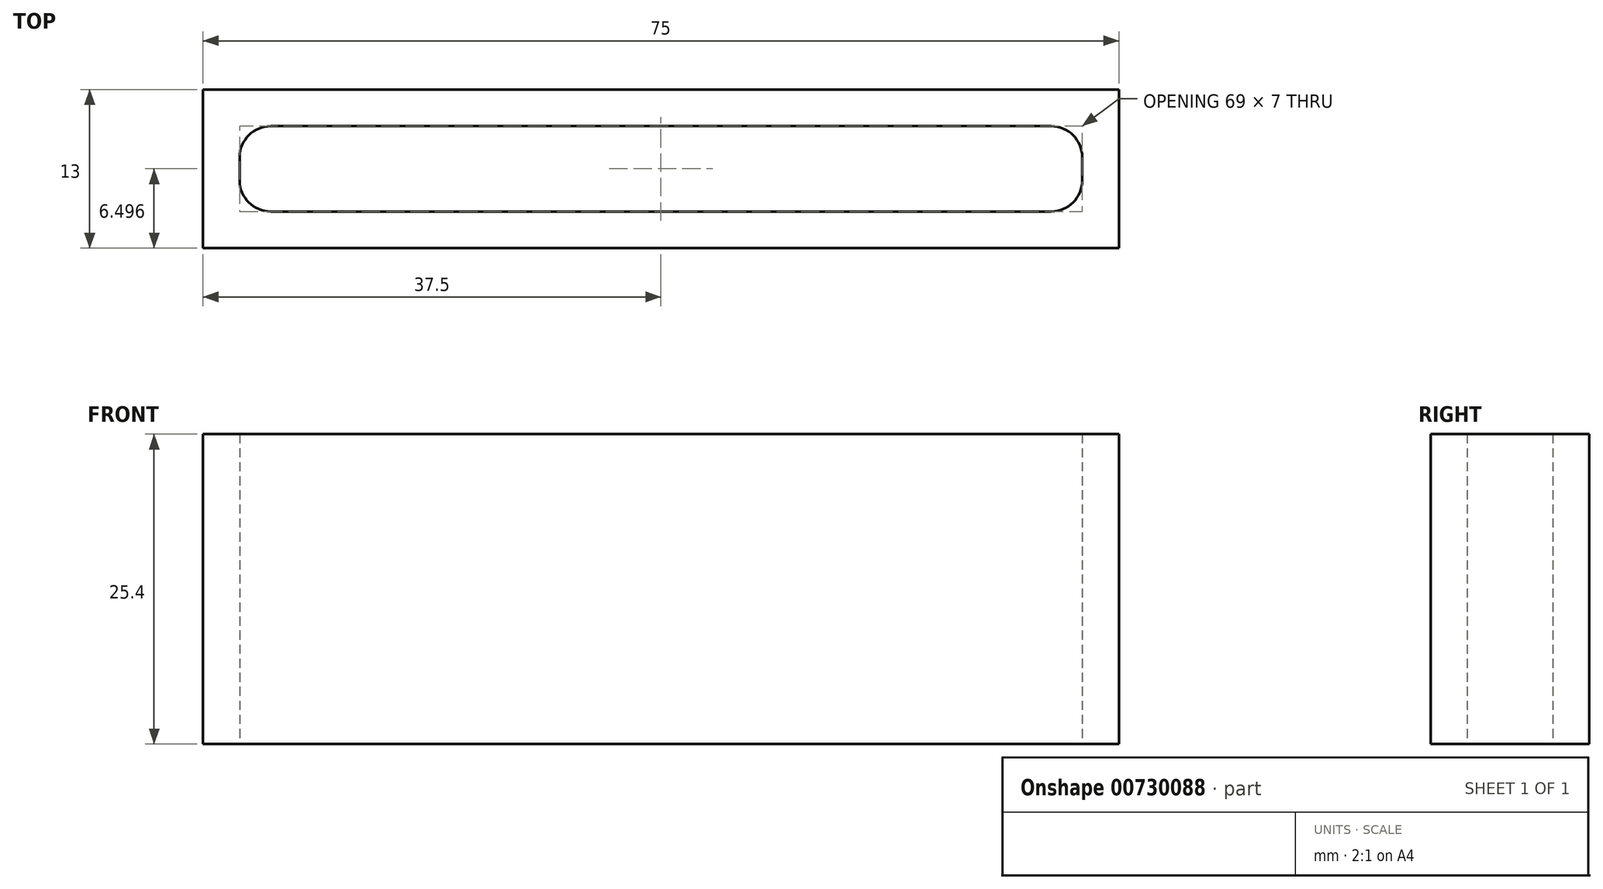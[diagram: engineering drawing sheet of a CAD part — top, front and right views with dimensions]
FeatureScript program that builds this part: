
annotation { "Feature Type Name" : "Feature", "Feature Type Description" : "" }
export const myFeature = defineFeature(function(context is Context, id is Id, definition is map)
    precondition{}
    {
        {
            var Q0;
            Q0=qCreatedBy(makeId("Top.planeOp"),FACE);
            var sketch = newSketch(context, id + "F0", { "sketchPlane" : qUnion([Q0])});
            skLineSegment(sketch, "E0.bottom", {"start": v(-1.66, -12.92) * mm, "end": v(62.26, -12.92) * mm});
            skLineSegment(sketch, "E0.top", {"start": v(-1.66, -5.92) * mm, "end": v(62.26, -5.92) * mm});
            skLineSegment(sketch, "E0.left", {"start": v(-4.2, -10.38) * mm, "end": v(-4.2, -8.46) * mm});
            skLineSegment(sketch, "E0.right", {"start": v(64.8, -10.38) * mm, "end": v(64.8, -8.46) * mm});
            skPoint(sketch, "E1.visualSharp", {"position": v(-4.2, -12.92) * mm});
            skArc(sketch, "E1.filletArc", {"start": v(-4.2, -10.38) * mm, "mid": v(-3.46, -12.18) * mm, "end": v(-1.66, -12.92) * mm});
            skPoint(sketch, "E2.visualSharp", {"position": v(-4.2, -5.92) * mm});
            skArc(sketch, "E2.filletArc", {"start": v(-1.66, -5.92) * mm, "mid": v(-3.46, -6.67) * mm, "end": v(-4.2, -8.46) * mm});
            skPoint(sketch, "E3.visualSharp", {"position": v(64.8, -12.92) * mm});
            skArc(sketch, "E3.filletArc", {"start": v(62.26, -12.92) * mm, "mid": v(64.06, -12.18) * mm, "end": v(64.8, -10.38) * mm});
            skPoint(sketch, "E4.visualSharp", {"position": v(64.8, -5.92) * mm});
            skArc(sketch, "E4.filletArc", {"start": v(64.8, -8.46) * mm, "mid": v(64.06, -6.67) * mm, "end": v(62.26, -5.92) * mm});
            skLineSegment(sketch, "E5", {"start": v(-1.66, -15.92) * mm, "end": v(-7.2, -15.92) * mm});
            skLineSegment(sketch, "E6", {"start": v(-7.2, -15.92) * mm, "end": v(-7.2, -12.92) * mm});
            skLineSegment(sketch, "E7.bottom", {"start": v(-1.66, -15.92) * mm, "end": v(67.8, -15.92) * mm});
            skLineSegment(sketch, "E7.top", {"start": v(-7.2, -2.92) * mm, "end": v(67.8, -2.92) * mm});
            skLineSegment(sketch, "E7.left", {"start": v(-7.2, -15.92) * mm, "end": v(-7.2, -2.92) * mm});
            skLineSegment(sketch, "E7.right", {"start": v(67.8, -15.92) * mm, "end": v(67.8, -2.92) * mm});
            skSolve(sketch);
        }
        {
            var Q0;
            Q0=makeQuery(id+"F0.imprint","IMPRINT",FACE,{"disambiguationData":[TD([[makeQuery(id+"F0.imprint","IMPRINT",EDGE,{"derivedFrom":sQuery(id+"F0.wireOp",EDGE,"E0.bottom")}),-1.0]])]});
            extrude(context, id + "F1", {"entities" : qUnion([Q0]), "depth" : 25.4 * mm, "offsetDistance" : 25.4 * mm});
        }
    });
